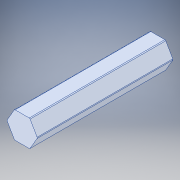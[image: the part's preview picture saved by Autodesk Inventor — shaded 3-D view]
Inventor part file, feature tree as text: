
AUTODESK INVENTOR PART (.ipt)
format: ipt  version: 2017 (Build 210142000, 142)  size: 132,608 bytes
history: native  units: in
note: dims shown in document units (in); Inventor stores cm internally (conversion verified against a paired STEP export)
features: extrude x1, sketch x1, projected_geometry x1, fillet x1
ambient origin geometry x8: Origin, YZ Plane, XZ Plane, XY Plane, X Axis, Y Axis, Z Axis, Center Point
bodies: Solid1 (feature_tree)
feature tree (4):
  extrude  "Extrusion1"  [1 undecoded]
  sketch  "Sketch1"  dims[d0=15.44in d1=0.0in]
  projected_geometry  "Projected Loop1"
  fillet  "Fillet1"  [1 undecoded]
note: 2 required parameter values undecoded (feature->parameter linkage not recoverable at this tier; creation-order binding heuristic only, values carry confidence <= 0.55)
